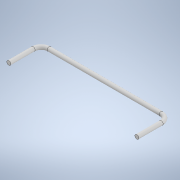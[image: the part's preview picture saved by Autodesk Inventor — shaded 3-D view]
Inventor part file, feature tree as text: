
AUTODESK INVENTOR PART (.ipt)
format: ipt  version: 2022 (Build 260153000, 153)  size: 110,592 bytes
history: native  units: in
note: dims shown in document units (in); Inventor stores cm internally (conversion verified against a paired STEP export)
features: sketch x2, other x1, sweep x1
ambient origin geometry x8: Origin, YZ Plane, XZ Plane, XY Plane, X Axis, Y Axis, Z Axis, Center Point
bodies: Body1 (feature_tree)
feature tree (4):
  other  "ソリッド1"
  sweep  "スイープ1"
  sketch  "スケッチ1"
  sketch  "スケッチ2"
